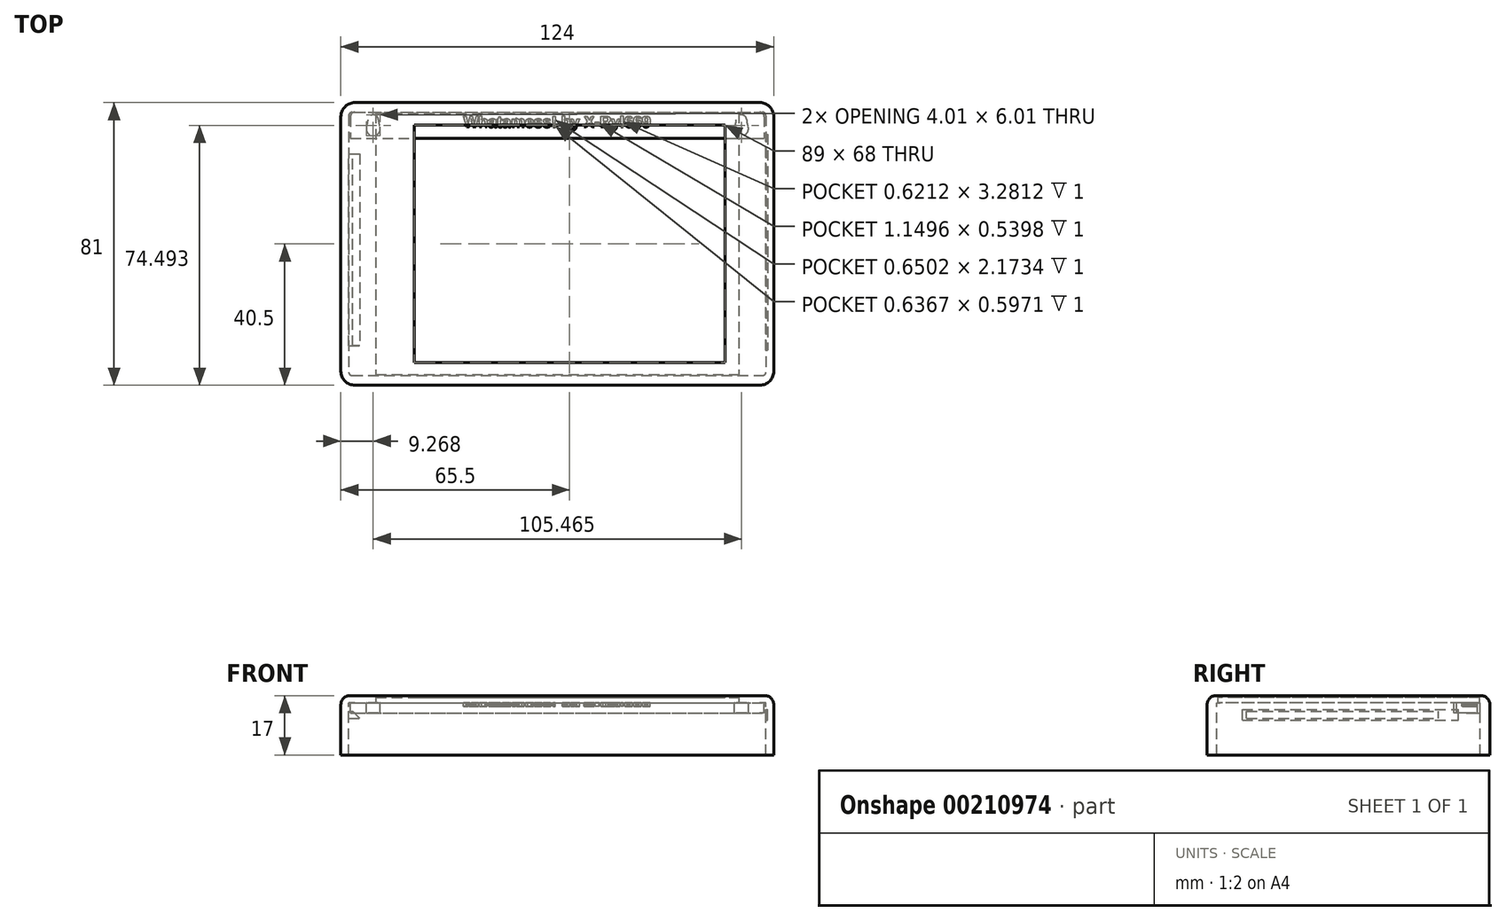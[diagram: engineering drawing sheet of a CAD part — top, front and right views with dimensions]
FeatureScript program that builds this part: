
annotation { "Feature Type Name" : "Feature", "Feature Type Description" : "" }
export const myFeature = defineFeature(function(context is Context, id is Id, definition is map)
    precondition{}
    {
        {
            var Q0;
            Q0=qCreatedBy(makeId("Top.planeOp"),FACE);
            var sketch = newSketch(context, id + "F0", { "sketchPlane" : qUnion([Q0])});
            skLineSegment(sketch, "E0.bottom", {"start": v(-52, 37.5) * mm, "end": v(52, 37.5) * mm});
            skLineSegment(sketch, "E0.top", {"start": v(-52, -37.5) * mm, "end": v(52, -37.5) * mm});
            skLineSegment(sketch, "E0.left", {"start": v(-52, 37.5) * mm, "end": v(-52, -37.5) * mm});
            skLineSegment(sketch, "E0.right", {"start": v(52, 37.5) * mm, "end": v(52, -37.5) * mm});
            skSolve(sketch);
        }
        {
            var Q0;
            Q0=qCreatedBy(makeId("Top.planeOp"),FACE);
            var sketch = newSketch(context, id + "F1", { "sketchPlane" : qUnion([Q0])});
            skLineSegment(sketch, "E1.bottom", {"start": v(-59.75, 37.75) * mm, "end": v(59.75, 37.75) * mm});
            skLineSegment(sketch, "E1.top", {"start": v(-59.75, -37.75) * mm, "end": v(59.75, -37.75) * mm});
            skLineSegment(sketch, "E1.left", {"start": v(-59.75, 37.75) * mm, "end": v(-59.75, -37.75) * mm});
            skLineSegment(sketch, "E1.right", {"start": v(59.75, 37.75) * mm, "end": v(59.75, -37.75) * mm});
            skPoint(sketch, "E1.middle", {"position": v(0, 0) * mm});
            skSolve(sketch);
        }
        {
            var Q0;
            Q0=qCreatedBy(makeId("Top.planeOp"),FACE);
            var sketch = newSketch(context, id + "F2", { "sketchPlane" : qUnion([Q0])});
            skLineSegment(sketch, "E2.bottom", {"start": v(-58, 40.5) * mm, "end": v(58, 40.5) * mm});
            skLineSegment(sketch, "E2.top", {"start": v(-58, -40.5) * mm, "end": v(58, -40.5) * mm});
            skLineSegment(sketch, "E2.left", {"start": v(-62, 36.5) * mm, "end": v(-62, -36.5) * mm});
            skLineSegment(sketch, "E2.right", {"start": v(62, 36.5) * mm, "end": v(62, -36.5) * mm});
            skPoint(sketch, "E2.middle", {"position": v(0, 0) * mm});
            skPoint(sketch, "E3.visualSharp", {"position": v(-62, 40.5) * mm});
            skArc(sketch, "E3.filletArc", {"start": v(-58, 40.5) * mm, "mid": v(-60.83, 39.33) * mm, "end": v(-62, 36.5) * mm});
            skPoint(sketch, "E4.visualSharp", {"position": v(62, 40.5) * mm});
            skArc(sketch, "E4.filletArc", {"start": v(62, 36.5) * mm, "mid": v(60.83, 39.33) * mm, "end": v(58, 40.5) * mm});
            skPoint(sketch, "E5.visualSharp", {"position": v(62, -40.5) * mm});
            skArc(sketch, "E5.filletArc", {"start": v(58, -40.5) * mm, "mid": v(60.83, -39.33) * mm, "end": v(62, -36.5) * mm});
            skPoint(sketch, "E6.visualSharp", {"position": v(-62, -40.5) * mm});
            skArc(sketch, "E6.filletArc", {"start": v(-62, -36.5) * mm, "mid": v(-60.83, -39.33) * mm, "end": v(-58, -40.5) * mm});
            skSolve(sketch);
        }
        {
            var Q0;
            Q0=qCreatedBy(makeId("Top.planeOp"),FACE);
            var sketch = newSketch(context, id + "F3", { "sketchPlane" : qUnion([Q0])});
            skLineSegment(sketch, "E7.bottom", {"start": v(-41, 34) * mm, "end": v(48, 34) * mm});
            skLineSegment(sketch, "E7.top", {"start": v(-41, -34) * mm, "end": v(48, -34) * mm});
            skLineSegment(sketch, "E7.left", {"start": v(-41, 34) * mm, "end": v(-41, -34) * mm});
            skLineSegment(sketch, "E7.right", {"start": v(48, 34) * mm, "end": v(48, -34) * mm});
            skPoint(sketch, "E7.middle", {"position": v(3.5, 0) * mm});
            skSolve(sketch);
        }
        {
            var Q0;
            Q0 = qSketchRegion(id + "F2", true);
            extrude(context, id + "F4", {"entities" : qUnion([Q0]), "depth" : 2 * mm, "hasSecondDirection" : true, "secondDirectionOppositeDirection" : true, "secondDirectionDepth" : 15 * mm});
        }
        {
            var Q0;
            Q0 = qSketchRegion(id + "F3", true);
            extrude(context, id + "F5", {"entities" : qUnion([Q0]), "operationType" : NewBodyOperationType.REMOVE, "depth" : 5 * mm});
        }
        {
            var Q0;
            Q0=makeQuery(id+"F4.opExtrude","CAP_EDGE",EDGE,{"disambiguationData":[OSD([sQuery(id+"F2.wireOp",EDGE,"E2.top")])],"isStart":false});
            fillet(context, id + "F6", {"entities" : qUnion([Q0]), "radius" : 2.5 * mm, "tangentPropagation" : true, "allowEdgeOverflow" : false});
        }
        {
            var Q0;
            Q0 = qSketchRegion(id + "F1", true);
            extrude(context, id + "F7", {"entities" : qUnion([Q0]), "operationType" : NewBodyOperationType.REMOVE, "oppositeDirection" : true, "depth" : 15 * mm});
        }
        {
            var Q0;
            Q0 = qSketchRegion(id + "F0", true);
            extrude(context, id + "F8", {"entities" : qUnion([Q0]), "operationType" : NewBodyOperationType.REMOVE, "depth" : 1.5 * mm});
        }
        {
            var Q0;
            Q0=qCreatedBy(makeId("Top.planeOp"),FACE);
            var sketch = newSketch(context, id + "F9", { "sketchPlane" : qUnion([Q0])});
            skLineSegment(sketch, "E8.bottom", {"start": v(-59.75, 25.78) * mm, "end": v(-56.63, 25.78) * mm});
            skLineSegment(sketch, "E8.top", {"start": v(-59.75, -29.22) * mm, "end": v(-56.63, -29.22) * mm});
            skLineSegment(sketch, "E8.left", {"start": v(-59.75, 25.78) * mm, "end": v(-59.75, -29.22) * mm});
            skLineSegment(sketch, "E8.right", {"start": v(-56.63, 25.78) * mm, "end": v(-56.63, -29.22) * mm});
            skSolve(sketch);
        }
        {
            var Q0;
            Q0 = qSketchRegion(id + "F9", true);
            extrude(context, id + "F10", {"entities" : qUnion([Q0]), "oppositeDirection" : true, "depth" : 2 * mm});
        }
        {
            var Q0;
            Q0=makeQuery(id+"F7.boolean.opBoolean","COPY",EDGE,{"derivedFrom":makeQuery(id+"F7.opExtrude","SWEPT_EDGE",EDGE,{"disambiguationData":[OSD([sQuery(id+"F1.wireOp",EDGE,"E1.bottom"),sQuery(id+"F1.wireOp",EDGE,"E1.left")])]})});
            cPoint(context, id + "F11", {"entities" : qUnion([Q0]), "parameter" : 0.5});
        }
        {
            var Q0;
            Q0=makeQuery(id+"F10.opExtrude","SWEPT_BODY",BODY,{"disambiguationData":[OSD([sQuery(id+"F9.wireOp",EDGE,"E8.bottom"),sQuery(id+"F9.wireOp",EDGE,"E8.top"),sQuery(id+"F9.wireOp",EDGE,"E8.left"),sQuery(id+"F9.wireOp",EDGE,"E8.right")])]});
            var Q1;
            Q1 = qCreatedBy(id + "F11" ,VERTEX);
            transform(context, id + "F12", {"entities" : qUnion([Q0]), "transformType" : TransformType.TRANSLATION_3D, "dx" : 0 * mm, "dy" : 0 * mm, "dz" : -2.5 * mm, "makeCopy" : false});
        }
        {
            var Q0;
            Q0=makeQuery(id+"F10.opExtrude","CAP_EDGE",EDGE,{"disambiguationData":[OSD([sQuery(id+"F9.wireOp",EDGE,"E8.right")])],"isStart":true});
            chamfer(context, id + "F13", {"entities" : qUnion([Q0]), "width" : 2 * mm, "tangentPropagation" : true});
        }
        {
            var Q0;
            Q0=qCreatedBy(makeId("Top.planeOp"),FACE);
            var sketch = newSketch(context, id + "F14", { "sketchPlane" : qUnion([Q0])});
            skLineSegment(sketch, "E9.bottom", {"start": v(57.6, 31.45) * mm, "end": v(60.25, 31.45) * mm});
            skLineSegment(sketch, "E9.top", {"start": v(57.6, -30.4) * mm, "end": v(60.25, -30.4) * mm});
            skLineSegment(sketch, "E9.left", {"start": v(57.6, 31.45) * mm, "end": v(57.6, -30.4) * mm});
            skLineSegment(sketch, "E9.right", {"start": v(60.25, 31.45) * mm, "end": v(60.25, -30.4) * mm});
            skSolve(sketch);
        }
        {
            var Q0;
            Q0 = qSketchRegion(id + "F14", true);
            extrude(context, id + "F15", {"entities" : qUnion([Q0]), "oppositeDirection" : true, "depth" : 3 * mm});
        }
        {
            var Q0;
            Q0=makeQuery(id+"F15.opExtrude","SWEPT_BODY",BODY,{"disambiguationData":[OSD([sQuery(id+"F14.wireOp",EDGE,"E9.bottom"),sQuery(id+"F14.wireOp",EDGE,"E9.top"),sQuery(id+"F14.wireOp",EDGE,"E9.left"),sQuery(id+"F14.wireOp",EDGE,"E9.right")])]});
            transform(context, id + "F16", {"entities" : qUnion([Q0]), "transformType" : TransformType.TRANSLATION_3D, "dx" : 0 * mm, "dy" : 0 * mm, "dz" : -2 * mm, "makeCopy" : false});
        }
        {
            var Q0;
            Q0=makeQuery(id+"F15.opExtrude","SWEPT_BODY",BODY,{"disambiguationData":[OSD([sQuery(id+"F14.wireOp",EDGE,"E9.bottom"),sQuery(id+"F14.wireOp",EDGE,"E9.top"),sQuery(id+"F14.wireOp",EDGE,"E9.left"),sQuery(id+"F14.wireOp",EDGE,"E9.right")])]});
            var Q1;
            Q1=makeQuery(id+"F4.opExtrude","SWEPT_BODY",BODY,{"disambiguationData":[OSD([sQuery(id+"F2.wireOp",EDGE,"E2.bottom"),sQuery(id+"F2.wireOp",EDGE,"E2.top"),sQuery(id+"F2.wireOp",EDGE,"E2.left"),sQuery(id+"F2.wireOp",EDGE,"E2.right"),sQuery(id+"F2.wireOp",EDGE,"E3.filletArc"),sQuery(id+"F2.wireOp",EDGE,"E4.filletArc"),sQuery(id+"F2.wireOp",EDGE,"E5.filletArc"),sQuery(id+"F2.wireOp",EDGE,"E6.filletArc")])]});
            booleanBodies(context, id + "F17", {"operationType" : BooleanOperationType.SUBTRACTION, "tools" : qUnion([Q0]), "targets" : qUnion([Q1])});
        }
        {
            var Q0;
            Q0=makeQuery(id+"F10.opExtrude","SWEPT_FACE",FACE,{"disambiguationData":[OSD([sQuery(id+"F9.wireOp",EDGE,"E8.left")])]});
            extrude(context, id + "F18", {"entities" : qUnion([Q0]), "operationType" : NewBodyOperationType.ADD, "depth" : 0.5 * mm});
        }
        {
            var Q0;
            Q0=makeQuery(id+"F7.boolean.opBoolean","COPY",EDGE,{"derivedFrom":makeQuery(id+"F7.opExtrude","SWEPT_EDGE",EDGE,{"disambiguationData":[OSD([sQuery(id+"F1.wireOp",EDGE,"E1.top"),sQuery(id+"F1.wireOp",EDGE,"E1.right")])]})});
            var Q1;
            Q1=makeQuery(id+"F7.boolean.opBoolean","COPY",EDGE,{"derivedFrom":makeQuery(id+"F7.opExtrude","SWEPT_EDGE",EDGE,{"disambiguationData":[OSD([sQuery(id+"F1.wireOp",EDGE,"E1.bottom"),sQuery(id+"F1.wireOp",EDGE,"E1.right")])]})});
            var Q2;
            Q2=makeQuery(id+"F7.boolean.opBoolean","COPY",EDGE,{"derivedFrom":makeQuery(id+"F7.opExtrude","SWEPT_EDGE",EDGE,{"disambiguationData":[OSD([sQuery(id+"F1.wireOp",EDGE,"E1.top"),sQuery(id+"F1.wireOp",EDGE,"E1.left")])]})});
            var Q3;
            Q3=makeQuery(id+"F7.boolean.opBoolean","COPY",EDGE,{"derivedFrom":makeQuery(id+"F7.opExtrude","SWEPT_EDGE",EDGE,{"disambiguationData":[OSD([sQuery(id+"F1.wireOp",EDGE,"E1.bottom"),sQuery(id+"F1.wireOp",EDGE,"E1.left")])]})});
            fillet(context, id + "F19", {"entities" : qUnion([Q0, Q1, Q2, Q3]), "radius" : 1 * mm, "tangentPropagation" : true, "allowEdgeOverflow" : false});
        }
        {
            var Q0;
            Q0=qCreatedBy(makeId("Top.planeOp"),FACE);
            var sketch = newSketch(context, id + "F20", { "sketchPlane" : qUnion([Q0])});
            skLineSegment(sketch, "E10.bottom", {"start": v(-58, 38) * mm, "end": v(58, 38) * mm, "construction": true});
            skLineSegment(sketch, "E10.top", {"start": v(-59.5, 30) * mm, "end": v(59.5, 30) * mm, "construction": true});
            skLineSegment(sketch, "E10.left", {"start": v(-59.5, 36.5) * mm, "end": v(-59.5, 30) * mm, "construction": true});
            skLineSegment(sketch, "E10.right", {"start": v(59.5, 36.5) * mm, "end": v(59.5, 30) * mm, "construction": true});
            skPoint(sketch, "E11.visualSharp", {"position": v(-59.5, 38) * mm});
            skArc(sketch, "E11.filletArc", {"start": v(-58, 38) * mm, "mid": v(-59.06, 37.56) * mm, "end": v(-59.5, 36.5) * mm, "construction": true});
            skPoint(sketch, "E12.visualSharp", {"position": v(59.5, 38) * mm});
            skArc(sketch, "E12.filletArc", {"start": v(59.5, 36.5) * mm, "mid": v(59.06, 37.56) * mm, "end": v(58, 38) * mm, "construction": true});
            skCircle(sketch, "E13", {"center": v(52.73, 35.5) * mm, "radius": 1.5 * mm});
            skCircle(sketch, "E14", {"center": v(52.73, 33) * mm, "radius": 2.01 * mm});
            skCircle(sketch, "E15.MirrorC", {"center": v(-52.73, 35.5) * mm, "radius": 1.5 * mm});
            skCircle(sketch, "E16.MirrorC", {"center": v(-52.73, 33) * mm, "radius": 2.01 * mm});
            skLineSegment(sketch, "E17.0", {"start": v(-59.25, 36.5) * mm, "end": v(-59.25, 30.25) * mm});
            skLineSegment(sketch, "E17.1", {"start": v(59.25, 36.5) * mm, "end": v(59.25, 30.25) * mm});
            skArc(sketch, "E17.2", {"start": v(59.25, 36.5) * mm, "mid": v(58.88, 37.38) * mm, "end": v(58, 37.75) * mm});
            skLineSegment(sketch, "E17.3", {"start": v(-59.25, 30.25) * mm, "end": v(59.25, 30.25) * mm});
            skLineSegment(sketch, "E17.4", {"start": v(-58, 37.75) * mm, "end": v(58, 37.75) * mm});
            skArc(sketch, "E17.5", {"start": v(-58, 37.75) * mm, "mid": v(-58.88, 37.38) * mm, "end": v(-59.25, 36.5) * mm});
            skSolve(sketch);
        }
        {
            var Q0;
            Q0 = qSketchRegion(id + "F20", true);
            extrude(context, id + "F21", {"entities" : qUnion([Q0]), "oppositeDirection" : true, "depth" : 3 * mm});
        }
        {
            var Q0;
            {var subQ0=sQuery(id+"F20.wireOp",EDGE,"E16.MirrorC");var subQ1=sQuery(id+"F20.wireOp",EDGE,"E15.MirrorC");Q0=makeQuery(id+"F21.opExtrude","SWEPT_EDGE",EDGE,{"disambiguationData":[OSD([subQ1,subQ0]),TDD([makeQuery(id+"F20.imprint","INTERSECT",VERTEX,{"disambiguationData":[OD(1.0)],"derivedFrom":[subQ1,subQ0]})])]});}
            var Q1;
            {var subQ0=sQuery(id+"F20.wireOp",EDGE,"E16.MirrorC");var subQ1=sQuery(id+"F20.wireOp",EDGE,"E15.MirrorC");Q1=makeQuery(id+"F21.opExtrude","SWEPT_EDGE",EDGE,{"disambiguationData":[OSD([subQ1,subQ0]),TDD([makeQuery(id+"F20.imprint","INTERSECT",VERTEX,{"disambiguationData":[OD(0.0)],"derivedFrom":[subQ1,subQ0]})])]});}
            var Q2;
            {var subQ0=sQuery(id+"F20.wireOp",EDGE,"E14");var subQ1=sQuery(id+"F20.wireOp",EDGE,"E13");Q2=makeQuery(id+"F21.opExtrude","SWEPT_EDGE",EDGE,{"disambiguationData":[OSD([subQ1,subQ0]),TDD([makeQuery(id+"F20.imprint","INTERSECT",VERTEX,{"disambiguationData":[OD(0.0)],"derivedFrom":[subQ1,subQ0]})])]});}
            var Q3;
            {var subQ0=sQuery(id+"F20.wireOp",EDGE,"E14");var subQ1=sQuery(id+"F20.wireOp",EDGE,"E13");Q3=makeQuery(id+"F21.opExtrude","SWEPT_EDGE",EDGE,{"disambiguationData":[OSD([subQ1,subQ0]),TDD([makeQuery(id+"F20.imprint","INTERSECT",VERTEX,{"disambiguationData":[OD(1.0)],"derivedFrom":[subQ1,subQ0]})])]});}
            fillet(context, id + "F22", {"entities" : qUnion([Q0, Q1, Q2, Q3]), "radius" : 5 * mm, "tangentPropagation" : true, "allowEdgeOverflow" : false});
        }
        {
            var Q0;
            Q0=qCreatedBy(makeId("Top.planeOp"),FACE);
            var sketch = newSketch(context, id + "F23", { "sketchPlane" : qUnion([Q0])});
            skText(sketch, "E18", { "text": "Whatamess! by X-Ryl669", "fontName": "Arimo-Bold.ttf"});
            const initialGuessF23  = {"E18": [-0.02685, 0.0335, 1, 0, 0.00326]};
            skSetInitialGuess(sketch, initialGuessF23);
            skSolve(sketch);
        }
        {
            var Q0;
            Q0 = qSketchRegion(id + "F23", true);
            extrude(context, id + "F24", {"entities" : qUnion([Q0]), "operationType" : NewBodyOperationType.REMOVE, "oppositeDirection" : true, "depth" : 1 * mm});
        }
    });
